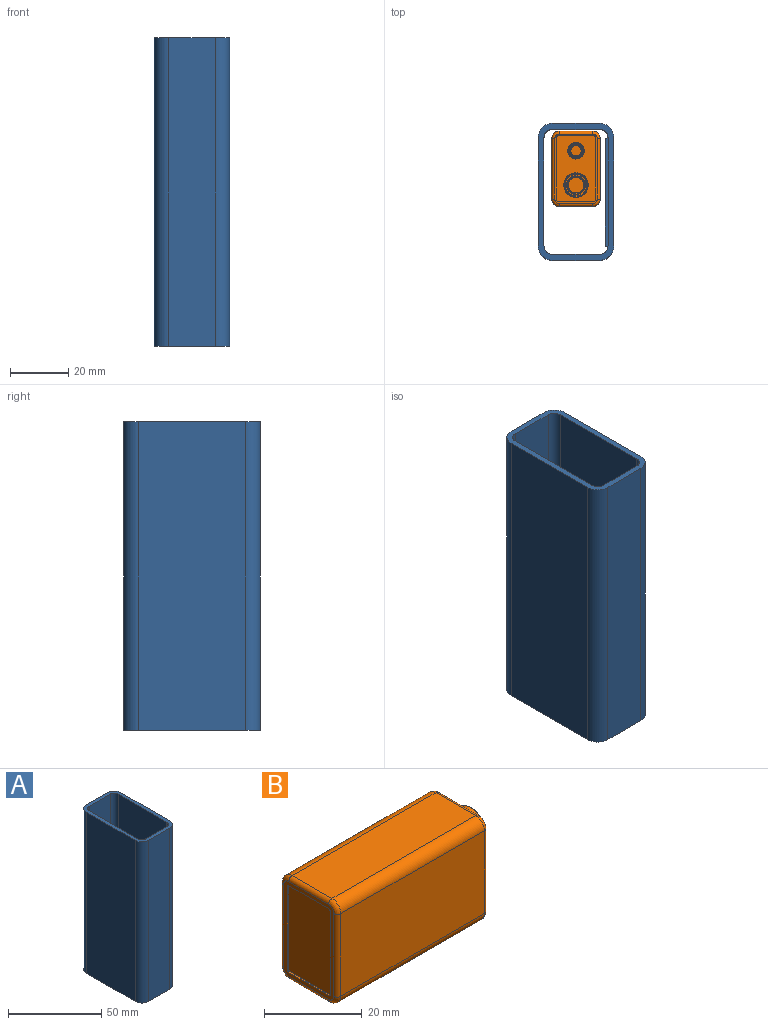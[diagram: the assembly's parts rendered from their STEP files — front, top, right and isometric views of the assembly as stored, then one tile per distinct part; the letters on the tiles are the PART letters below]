
ASSEMBLY  parts=2 mates=1
PART A: 24 faces, bbox 26x47x106 mm
  f0: plane 101.5x37mm, normal (-1,0,0), area 3755.5mm2, adj f1,f17,f18,f21
  f1: plane 47x26mm, normal (0,0,1), area 262.3mm2, adj f0,f3,f4,f5,f6,f7,f8,f9
  f2: plane 47x26mm, normal (0,0,-1), area 262.3mm2, adj f3,f4,f5,f6,f7,f8,f9,f10
  f3: plane 106x16mm, normal (0,1,0), area 1696mm2, adj f1,f2,f7,f10
  f4: plane 106x37mm, normal (-1,0,0), area 3922mm2, adj f1,f2,f7,f8
  f5: plane 106x16mm, normal (0,-1,0), area 1696mm2, adj f1,f2,f8,f9
  f6: plane 106x37mm, normal (1,0,0), area 3922mm2, adj f1,f2,f9,f10
  f7: cylinder r=5mm len=106mm, axis (0,0,1), area 832.5mm2, adj f1,f2,f3,f4
  f8: cylinder r=5mm len=106mm, axis (0,0,-1), area 832.5mm2, adj f1,f2,f4,f5
  f9: cylinder r=5mm len=106mm, axis (0,0,1), area 832.5mm2, adj f1,f2,f5,f6
  f10: cylinder r=5mm len=106mm, axis (0,0,-1), area 832.5mm2, adj f1,f2,f3,f6
  f11: plane 106x16mm, normal (0,-1,0), area 1696mm2, adj f1,f2,f15,f18
  f12: plane 106x37mm, normal (1,0,0), area 3922mm2, adj f1,f2,f15,f16
  f13: plane 106x16mm, normal (0,1,0), area 1696mm2, adj f1,f2,f16,f17
  f14: plane 37x2.5mm, normal (-1,0,0), area 92.5mm2, adj f2,f17,f18,f19
  f15: cylinder r=3mm len=106mm, axis (0,0,1), area 499.5mm2, adj f1,f2,f11,f12
  f16: cylinder r=3mm len=106mm, axis (0,0,-1), area 499.5mm2, adj f1,f2,f12,f13
  f17: cylinder r=3mm len=106mm, axis (0,0,1), area 499.5mm2, adj f0,f1,f2,f13,f14,f20
  f18: cylinder r=3mm len=106mm, axis (0,0,-1), area 499.5mm2, adj f0,f1,f2,f11,f14,f22
  f19: plane 37x1mm, normal (0,0,-1), area 37mm2, adj f14,f20,f22,f23
  f20: plane 2x1mm, normal (0,-1,0), area 2mm2, adj f17,f19,f21,f23
  f21: plane 37x1mm, normal (0,0,1), area 37mm2, adj f0,f20,f22,f23
  f22: plane 2x1mm, normal (0,1,0), area 2mm2, adj f18,f19,f21,f23
  f23: plane 37x2mm, normal (-1,0,0), area 74mm2, adj f19,f20,f21,f22
PART B: 74 faces, bbox 47.3x17x26.1 mm
  f0: plane 21.79x12.52mm, normal (-1,0,0), area 272.7mm2, adj f1,f2,f3,f4,f5,f6,f7,f8
  f1: cylinder r=0.51mm len=0.51mm, axis (-1,0,0), area 0.3mm2, adj f0,f2,f8,f10
  f2: plane 20.78x0.38mm, normal (0,-1,0), area 7.9mm2, adj f0,f1,f3,f10
  f3: cylinder r=0.51mm len=0.51mm, axis (-1,0,0), area 0.3mm2, adj f0,f2,f4,f10
  f4: plane 11.51x0.38mm, normal (0,0,-1), area 4.4mm2, adj f0,f3,f5,f10
  f5: cylinder r=0.51mm len=0.51mm, axis (-1,0,0), area 0.3mm2, adj f0,f4,f6,f10
  f6: plane 20.78x0.38mm, normal (0,1,0), area 7.9mm2, adj f0,f5,f7,f10
  f7: cylinder r=0.51mm len=0.51mm, axis (-1,0,0), area 0.3mm2, adj f0,f6,f8,f10
  f8: plane 11.51x0.38mm, normal (0,0,1), area 4.4mm2, adj f0,f1,f7,f10
  f9: plane 3.56x3.56mm, normal (1,0,0), area 9.8mm2, adj f11,f12
  f10: plane 23.84x14.57mm, normal (-1,0,0), area 72mm2, adj f1,f2,f3,f4,f5,f6,f7,f8
  f11: bspline ~4.07x4.07mm, area 2.4mm2, adj f9,f12,f21
  f12: bspline ~4.07x4.07mm, area 2.4mm2, adj f9,f11,f21
  f13: bspline ~2.6x2.6mm, area 5.4mm2, adj f10,f14,f20,f22
  f14: cylinder r=1.02mm len=20.78mm, axis (0,0,1), area 33.2mm2, adj f10,f13,f15,f23
  f15: bspline ~2.6x2.6mm, area 5.4mm2, adj f10,f14,f16,f24
  f16: cylinder r=1.02mm len=11.51mm, axis (0,1,0), area 18.4mm2, adj f10,f15,f17,f25
  f17: bspline ~2.6x2.6mm, area 5.4mm2, adj f10,f16,f18,f26
  f18: cylinder r=1.02mm len=20.78mm, axis (0,0,-1), area 33.2mm2, adj f10,f17,f19,f27
  f19: bspline ~2.6x2.6mm, area 5.4mm2, adj f10,f18,f20,f28
  f20: cylinder r=1.02mm len=11.51mm, axis (0,-1,0), area 18.4mm2, adj f10,f13,f19,f29
  f21: cylinder r=2.02mm len=4.04mm, axis (1,0,0), area 35.4mm2, adj f11,f12,f30,f31
  f22: cylinder r=2.54mm len=41.68mm, axis (-1,0,0), area 166.3mm2, adj f13,f23,f29,f32
  f23: plane 41.68x20.78mm, normal (0,-1,0), area 866mm2, adj f14,f22,f24,f33
  f24: cylinder r=2.54mm len=41.68mm, axis (-1,0,0), area 166.3mm2, adj f15,f23,f25,f34
  f25: plane 41.68x11.51mm, normal (0,0,1), area 479.6mm2, adj f16,f24,f26,f35
  f26: cylinder r=2.54mm len=41.68mm, axis (-1,0,0), area 166.3mm2, adj f17,f25,f27,f36
  f27: plane 41.68x20.78mm, normal (0,1,0), area 866mm2, adj f18,f26,f28,f37
  f28: cylinder r=2.54mm len=41.68mm, axis (-1,0,0), area 166.3mm2, adj f19,f27,f29,f38
  f29: plane 41.68x11.51mm, normal (0,0,-1), area 479.6mm2, adj f20,f22,f28,f39
  f30: bspline ~4.6x4.6mm, area 2.6mm2, adj f21,f31,f40
  f31: bspline ~4.6x4.6mm, area 2.6mm2, adj f21,f30,f40
  f32: bspline ~2.6x2.6mm, area 5.4mm2, adj f22,f33,f39,f41
  f33: cylinder r=1.02mm len=20.78mm, axis (0,0,-1), area 33.2mm2, adj f23,f32,f34,f41
  f34: bspline ~2.6x2.6mm, area 5.4mm2, adj f24,f33,f35,f41
  f35: cylinder r=1.02mm len=11.51mm, axis (0,-1,0), area 18.4mm2, adj f25,f34,f36,f41
  f36: bspline ~2.6x2.6mm, area 5.4mm2, adj f26,f35,f37,f41
  f37: cylinder r=1.02mm len=20.78mm, axis (0,0,1), area 33.2mm2, adj f27,f36,f38,f41
  f38: bspline ~2.6x2.6mm, area 5.4mm2, adj f28,f37,f39,f41
  f39: cylinder r=1.02mm len=11.51mm, axis (0,1,0), area 18.4mm2, adj f29,f32,f38,f41
  f40: plane 5.17x5.17mm, normal (1,0,0), area 4.4mm2, adj f30,f31,f42,f43
  f41: plane 23.84x14.57mm, normal (1,0,0), area 45.2mm2, adj f32,f33,f34,f35,f36,f37,f38,f39
  f42: bspline ~5.67x5.67mm, area 3.4mm2, adj f40,f43,f52
  f43: bspline ~5.67x5.67mm, area 3.4mm2, adj f40,f42,f52
  f44: plane 21.54x0.38mm, normal (0,-1,0), area 8.2mm2, adj f41,f45,f51,f53
  f45: cylinder r=0.51mm len=0.51mm, axis (1,0,0), area 0.3mm2, adj f41,f44,f46,f53
  f46: plane 12.27x0.38mm, normal (0,0,1), area 4.7mm2, adj f41,f45,f47,f53
  f47: cylinder r=0.51mm len=0.51mm, axis (1,0,0), area 0.3mm2, adj f41,f46,f48,f53
  f48: plane 21.54x0.38mm, normal (0,1,0), area 8.2mm2, adj f41,f47,f49,f53
  f49: cylinder r=0.51mm len=0.51mm, axis (1,0,0), area 0.3mm2, adj f41,f48,f50,f53
  f50: plane 12.27x0.38mm, normal (0,0,-1), area 4.7mm2, adj f41,f49,f51,f53
  f51: cylinder r=0.51mm len=0.51mm, axis (1,0,0), area 0.3mm2, adj f41,f44,f50,f53
  f52: cylinder r=2.82mm len=5.64mm, axis (-1,0,0), area 63mm2, adj f42,f43,f53
  f53: plane 22.56x13.28mm, normal (1,0,0), area 243.8mm2, adj f44,f45,f46,f47,f48,f49,f50,f51
  f54: plane 5.43x5.43mm, normal (1,0,0), area 22.8mm2, adj f56,f57
  f55: cylinder r=3.12mm len=6.25mm, axis (-1,0,0), area 34.9mm2, adj f53,f58
  f56: bspline ~5.93x5.93mm, area 3.6mm2, adj f54,f57,f59
  f57: bspline ~5.93x5.93mm, area 3.6mm2, adj f54,f56,f59
  f58: plane 8.02x8.02mm, normal (-1,0,0), area 19.1mm2, adj f55,f60,f61
  f59: cylinder r=2.95mm len=5.89mm, axis (1,0,0), area 18.8mm2, adj f56,f57,f63,f64
  f60: bspline ~8.49x8.49mm, area 5.2mm2, adj f58,f61,f65
  f61: bspline ~8.49x8.49mm, area 5.2mm2, adj f58,f60,f65
  f62: bspline ~7.96x7.96mm, area 4.9mm2, adj f66,f70,f72
  f63: bspline ~6.45x6.45mm, area 3.8mm2, adj f59,f64,f66
  f64: bspline ~6.45x6.45mm, area 3.8mm2, adj f59,f63,f66
  f65: cylinder r=4.23mm len=8.46mm, axis (-1,0,0), area 43.9mm2, adj f60,f61,f67,f68
  f66: plane 7.48x7.48mm, normal (1,0,0), area 11mm2, adj f62,f63,f64,f70
  f67: bspline ~8.47x8.47mm, area 2.6mm2, adj f65,f68,f71
  f68: bspline ~8.47x8.47mm, area 2.6mm2, adj f65,f67,f71
  f69: bspline ~8.2x8.2mm, area 2.5mm2, adj f71,f72,f73
  f70: bspline ~7.96x7.96mm, area 4.9mm2, adj f62,f66,f72
  f71: plane 8.27x8.27mm, normal (1,0,0), area 0.3mm2, adj f67,f68,f69,f73
  f72: cylinder r=3.96mm len=7.92mm, axis (1,0,0), area 34.8mm2, adj f62,f69,f70,f73
  f73: bspline ~8.2x8.2mm, area 2.5mm2, adj f69,f71,f72
PLACE A t=(-22.69,-6.06,34.52)mm fixed
PLACE B rot(axis=(0.58,-0.58,0.58),120deg) t=(-14.88,-11.35,34.52)mm
MATE fastened A.f2 <-> B.f10  axis (0,0,-1) through (-23.17,15.09,34.52)mm
